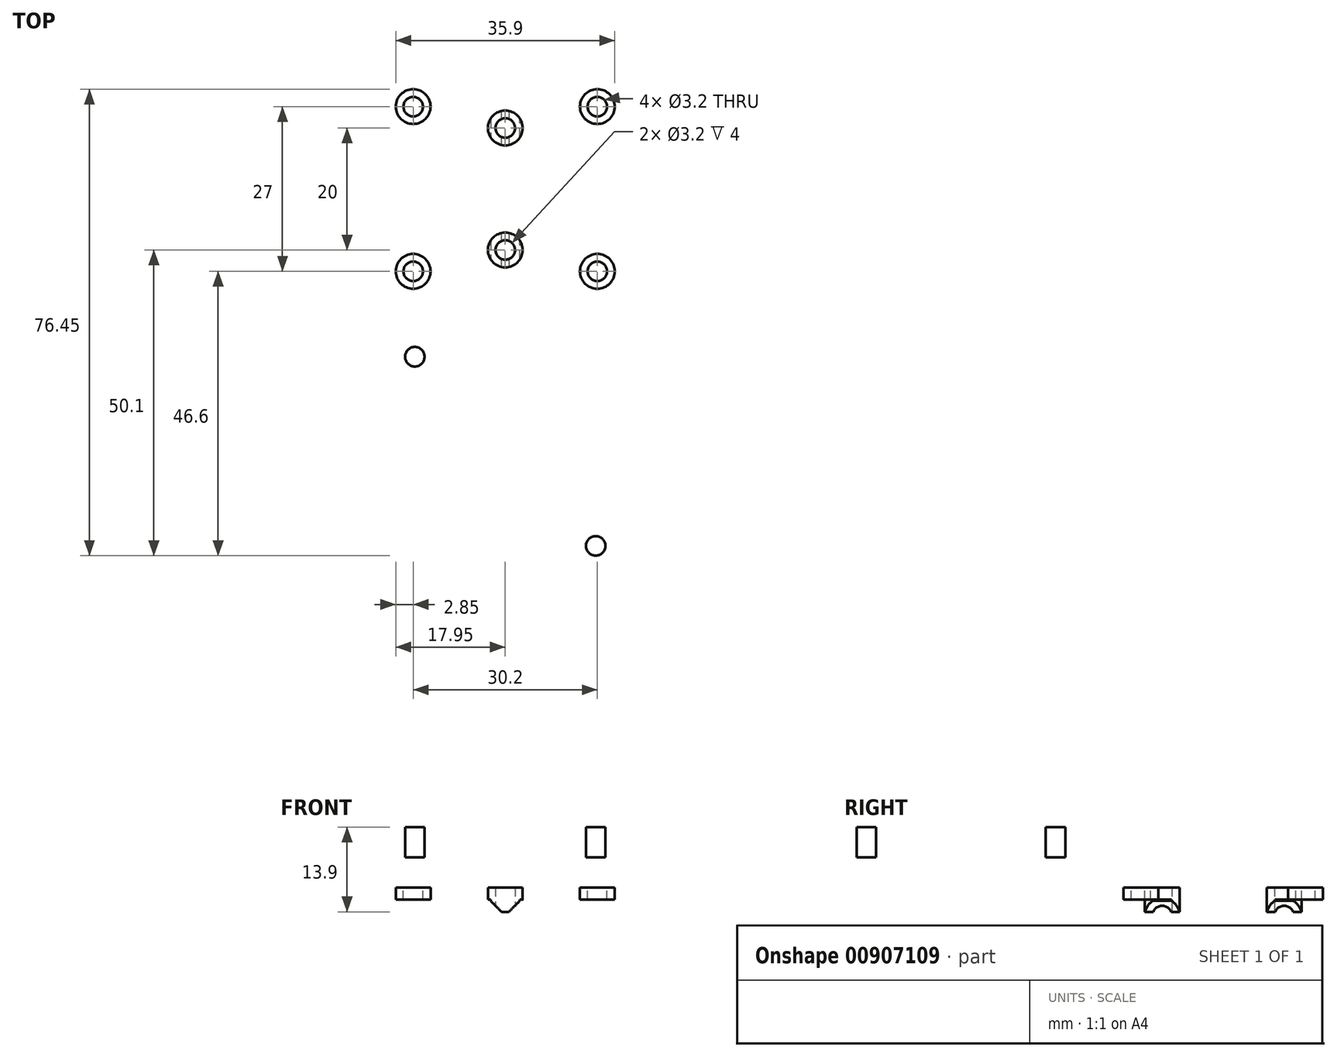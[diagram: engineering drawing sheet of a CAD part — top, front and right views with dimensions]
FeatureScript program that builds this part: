
annotation { "Feature Type Name" : "Feature", "Feature Type Description" : "" }
export const myFeature = defineFeature(function(context is Context, id is Id, definition is map)
    precondition{}
    {
        {
            var Q0;
            Q0=qCreatedBy(makeId("Top.planeOp"),FACE);
            var sketch = newSketch(context, id + "F0", { "sketchPlane" : qUnion([Q0])});
            skLineSegment(sketch, "E0.bottom", {"start": v(0, 0) * mm, "end": v(40.2, 0) * mm});
            skLineSegment(sketch, "E0.top", {"start": v(0, 40) * mm, "end": v(40.2, 40) * mm});
            skLineSegment(sketch, "E0.left", {"start": v(0, 0) * mm, "end": v(0, 40) * mm});
            skLineSegment(sketch, "E0.right", {"start": v(40.2, 0) * mm, "end": v(40.2, 40) * mm});
            skSolve(sketch);
        }
        {
            var Q0;
            Q0=qSketchRegion(id+"F0",true);
            extrude(context, id + "F1", {"entities" : qUnion([Q0]), "depth" : 5.5 * mm, "offsetDistance" : 25 * mm});
        }
        {
            var Q0;
            Q0=makeQuery(id+"F1.opExtrude","CAP_FACE",FACE,{"disambiguationData":[OSD([sQuery(id+"F0.wireOp",EDGE,"E0.bottom"),sQuery(id+"F0.wireOp",EDGE,"E0.top"),sQuery(id+"F0.wireOp",EDGE,"E0.left"),sQuery(id+"F0.wireOp",EDGE,"E0.right")])],"isStart":false});
            var sketch = newSketch(context, id + "F2", { "sketchPlane" : qUnion([Q0])});
            skLineSegment(sketch, "E1", {"start": v(0, 20) * mm, "end": v(40.2, 20) * mm, "construction": true});
            skLineSegment(sketch, "E2", {"start": v(35.2, 40) * mm, "end": v(35.2, 0) * mm, "construction": true});
            skLineSegment(sketch, "E3", {"start": v(0, 6.5) * mm, "end": v(40.2, 6.5) * mm, "construction": true});
            skLineSegment(sketch, "E4", {"start": v(40.2, 33.5) * mm, "end": v(0, 33.5) * mm, "construction": true});
            skCircle(sketch, "E5", {"center": v(35.2, 6.5) * mm, "radius": 2.85 * mm});
            skCircle(sketch, "E6", {"center": v(35.2, 33.5) * mm, "radius": 2.85 * mm});
            skLineSegment(sketch, "E7", {"start": v(20.1, 40) * mm, "end": v(20.1, 0) * mm, "construction": true});
            skCircle(sketch, "E8.MirrorC", {"center": v(5, 33.5) * mm, "radius": 2.85 * mm});
            skCircle(sketch, "E9.MirrorC", {"center": v(5, 6.5) * mm, "radius": 2.85 * mm});
            skSolve(sketch);
        }
        {
            var Q0;
            Q0=qSketchRegion(id+"F2",true);
            extrude(context, id + "F3", {"entities" : qUnion([Q0]), "operationType" : NewBodyOperationType.REMOVE, "oppositeDirection" : true, "depth" : 3.5 * mm, "offsetDistance" : 25 * mm});
        }
        {
            var Q0;
            Q0=makeQuery(id+"F2.imprint","IMPRINT",FACE,{"disambiguationData":[TD([[makeQuery(id+"F2.imprint","IMPRINT",EDGE,{"derivedFrom":sQuery(id+"F2.wireOp",EDGE,"E5")}),-1.0]])]});
            var sketch = newSketch(context, id + "F4", { "sketchPlane" : qUnion([Q0])});
            skCircle(sketch, "E10", {"center": v(35.2, 33.5) * mm, "radius": 1.6 * mm});
            skCircle(sketch, "E11", {"center": v(35.2, 6.5) * mm, "radius": 1.6 * mm});
            skCircle(sketch, "E12.MirrorC", {"center": v(5, 33.5) * mm, "radius": 1.6 * mm});
            skCircle(sketch, "E13.MirrorC", {"center": v(5, 6.5) * mm, "radius": 1.6 * mm});
            skSolve(sketch);
        }
        {
            var Q0;
            Q0=qSketchRegion(id+"F4",true);
            extrude(context, id + "F5", {"entities" : qUnion([Q0]), "operationType" : NewBodyOperationType.REMOVE, "oppositeDirection" : true, "depth" : 25 * mm, "offsetDistance" : 25 * mm});
        }
        {
            var Q0;
            Q0=makeQuery(id+"F1.opExtrude","CAP_FACE",FACE,{"disambiguationData":[OSD([sQuery(id+"F0.wireOp",EDGE,"E0.bottom"),sQuery(id+"F0.wireOp",EDGE,"E0.top"),sQuery(id+"F0.wireOp",EDGE,"E0.left"),sQuery(id+"F0.wireOp",EDGE,"E0.right")])],"isStart":true});
            var sketch = newSketch(context, id + "F6", { "sketchPlane" : qUnion([Q0])});
            skLineSegment(sketch, "E14.bottom", {"start": v(17.7, 0) * mm, "end": v(22.5, 0) * mm});
            skLineSegment(sketch, "E14.top", {"start": v(17.7, -40) * mm, "end": v(22.5, -40) * mm});
            skLineSegment(sketch, "E14.left", {"start": v(22.5, 0) * mm, "end": v(22.5, -40) * mm});
            skLineSegment(sketch, "E14.right", {"start": v(17.7, 0) * mm, "end": v(17.7, -40) * mm});
            skSolve(sketch);
        }
        {
            var Q0;
            Q0=qSketchRegion(id+"F6",true);
            extrude(context, id + "F7", {"entities" : qUnion([Q0]), "operationType" : NewBodyOperationType.ADD, "depth" : 2 * mm, "offsetDistance" : 25 * mm});
        }
        {
            var Q0;
            Q0=makeQuery(id+"F7.opExtrude","CAP_EDGE",EDGE,{"disambiguationData":[OSD([sQuery(id+"F6.wireOp",EDGE,"E14.right")])],"isStart":false});
            var Q1;
            Q1=makeQuery(id+"F7.opExtrude","CAP_EDGE",EDGE,{"disambiguationData":[OSD([sQuery(id+"F6.wireOp",EDGE,"E14.left")])],"isStart":false});
            chamfer(context, id + "F8", {"entities" : qUnion([Q0, Q1]), "width" : 1.8 * mm, "tangentPropagation" : true});
        }
        {
            var Q0;
            Q0=makeQuery(id+"F7.opExtrude","CAP_FACE",FACE,{"disambiguationData":[OSD([sQuery(id+"F6.wireOp",EDGE,"E14.bottom"),sQuery(id+"F6.wireOp",EDGE,"E14.top"),sQuery(id+"F6.wireOp",EDGE,"E14.left"),sQuery(id+"F6.wireOp",EDGE,"E14.right")])],"isStart":false});
            var sketch = newSketch(context, id + "F9", { "sketchPlane" : qUnion([Q0])});
            skCircle(sketch, "E15", {"center": v(20.1, -30) * mm, "radius": 1.6 * mm});
            skLineSegment(sketch, "E16", {"start": v(20.1, 0) * mm, "end": v(20.1, -40) * mm, "construction": true});
            skLineSegment(sketch, "E17", {"start": v(20.7, -30) * mm, "end": v(19.5, -30) * mm, "construction": true});
            skLineSegment(sketch, "E18", {"start": v(20.7, -10) * mm, "end": v(19.5, -10) * mm, "construction": true});
            skPoint(sketch, "E19", {"position": v(20.1, -10) * mm});
            skCircle(sketch, "E20", {"center": v(20.1, -10) * mm, "radius": 1.6 * mm});
            skSolve(sketch);
        }
        {
            var Q0;
            Q0=qSketchRegion(id+"F9",true);
            extrude(context, id + "F10", {"entities" : qUnion([Q0]), "operationType" : NewBodyOperationType.REMOVE, "oppositeDirection" : true, "depth" : 25 * mm, "offsetDistance" : 25 * mm});
        }
        {
            var Q0;
            Q0=makeQuery(id+"F2.imprint","IMPRINT",FACE,{"disambiguationData":[TD([[makeQuery(id+"F2.imprint","IMPRINT",EDGE,{"derivedFrom":sQuery(id+"F2.wireOp",EDGE,"E5")}),-1.0]])]});
            var sketch = newSketch(context, id + "F11", { "sketchPlane" : qUnion([Q0])});
            skCircle(sketch, "E21", {"center": v(20.1, 30) * mm, "radius": 2.85 * mm});
            skCircle(sketch, "E22.MirrorC", {"center": v(20.1, 10) * mm, "radius": 2.85 * mm});
            skSolve(sketch);
        }
        {
            var Q0;
            Q0=qSketchRegion(id+"F11",true);
            extrude(context, id + "F12", {"entities" : qUnion([Q0]), "operationType" : NewBodyOperationType.REMOVE, "oppositeDirection" : true, "depth" : 3.5 * mm, "offsetDistance" : 25 * mm});
        }
        {
            var Q0;
            Q0=makeQuery(id+"F2.imprint","IMPRINT",FACE,{"disambiguationData":[TD([[makeQuery(id+"F2.imprint","IMPRINT",EDGE,{"derivedFrom":sQuery(id+"F2.wireOp",EDGE,"E5")}),-1.0]])]});
            extrude(context, id + "F13", {"entities" : qUnion([Q0]), "operationType" : NewBodyOperationType.ADD, "depth" : 6.4 * mm, "offsetDistance" : 25 * mm});
        }
        {
            var Q0;
            Q0 = qSketchRegion(id + "F11", true);
            extrude(context, id + "F14", {"entities" : qUnion([Q0]), "operationType" : NewBodyOperationType.REMOVE, "oppositeDirection" : true, "depth" : -25 * mm, "offsetDistance" : 25 * mm});
        }
        {
            var Q0;
            {var subQ0=sQuery(id+"F0.wireOp",EDGE,"E0.bottom");Q0=makeQuery(id+"F13.boolean.opBoolean","MERGE",FACE,{"derivedFrom":[makeQuery(id+"F7.boolean.opBoolean","MERGE",FACE,{"derivedFrom":[makeQuery(id+"F1.opExtrude","SWEPT_FACE",FACE,{"disambiguationData":[OSD([subQ0])]}),makeQuery(id+"F7.opExtrude","SWEPT_FACE",FACE,{"disambiguationData":[OSD([sQuery(id+"F6.wireOp",EDGE,"E14.bottom")])]})]}),makeQuery(id+"F13.opExtrude","SWEPT_FACE",FACE,{"disambiguationData":[OSD([subQ0])]})]});}
            var sketch = newSketch(context, id + "F15", { "sketchPlane" : qUnion([Q0])});
            skLineSegment(sketch, "E23.bottom", {"start": v(40.2, 11.9) * mm, "end": v(0, 11.9) * mm});
            skLineSegment(sketch, "E23.top", {"start": v(40.2, 6.9) * mm, "end": v(0, 6.9) * mm});
            skLineSegment(sketch, "E23.left", {"start": v(40.2, 11.9) * mm, "end": v(40.2, 6.9) * mm});
            skLineSegment(sketch, "E23.right", {"start": v(0, 11.9) * mm, "end": v(0, 6.9) * mm});
            skSolve(sketch);
        }
        {
            var Q0;
            Q0=makeQuery(id+"F15.imprint","IMPRINT",FACE,{"disambiguationData":[TD([[makeQuery(id+"F15.imprint","IMPRINT",EDGE,{"derivedFrom":sQuery(id+"F15.wireOp",EDGE,"E23.bottom")}),-1.0]])]});
            extrude(context, id + "F16", {"entities" : qUnion([Q0]), "operationType" : NewBodyOperationType.ADD, "depth" : 44 * mm, "offsetDistance" : 25 * mm});
        }
        {
            var Q0;
            Q0=makeQuery(id+"F16.boolean.opBoolean","MERGE",FACE,{"derivedFrom":[makeQuery(id+"F13.opExtrude","CAP_FACE",FACE,{"disambiguationData":[OSD([sQuery(id+"F0.wireOp",EDGE,"E0.bottom"),sQuery(id+"F0.wireOp",EDGE,"E0.top"),sQuery(id+"F0.wireOp",EDGE,"E0.left"),sQuery(id+"F0.wireOp",EDGE,"E0.right"),sQuery(id+"F2.wireOp",EDGE,"E5"),sQuery(id+"F2.wireOp",EDGE,"E6"),sQuery(id+"F2.wireOp",EDGE,"E8.MirrorC"),sQuery(id+"F2.wireOp",EDGE,"E9.MirrorC")])],"isStart":false}),makeQuery(id+"F16.opExtrude","SWEPT_FACE",FACE,{"disambiguationData":[OSD([sQuery(id+"F15.wireOp",EDGE,"E23.bottom")])]})]});
            var sketch = newSketch(context, id + "F17", { "sketchPlane" : qUnion([Q0])});
            skLineSegment(sketch, "E24", {"start": v(40.2, -2) * mm, "end": v(0, -2) * mm, "construction": true});
            skLineSegment(sketch, "E25", {"start": v(0, -44) * mm, "end": v(40.2, -2) * mm, "construction": true});
            skLineSegment(sketch, "E26", {"start": v(0, -2) * mm, "end": v(40.2, -44) * mm, "construction": true});
            skCircle(sketch, "E27", {"center": v(20.1, -23) * mm, "radius": 11.1 * mm});
            skCircle(sketch, "E28", {"center": v(5.26, -38.5) * mm, "radius": 1.6 * mm});
            skLineSegment(sketch, "E29", {"start": v(40.2, -23) * mm, "end": v(0, -23) * mm, "construction": true});
            skLineSegment(sketch, "E30", {"start": v(20.1, -44) * mm, "end": v(20.1, -2) * mm, "construction": true});
            skCircle(sketch, "E31.MirrorC", {"center": v(34.94, -38.5) * mm, "radius": 1.6 * mm});
            skCircle(sketch, "E32.MirrorC", {"center": v(5.26, -7.5) * mm, "radius": 1.6 * mm});
            skCircle(sketch, "E33.MirrorC", {"center": v(34.94, -7.5) * mm, "radius": 1.6 * mm});
            skSolve(sketch);
        }
        {
            var Q0;
            Q0=makeQuery(id+"F17.imprint","IMPRINT",FACE,{"disambiguationData":[TD([[makeQuery(id+"F17.imprint","IMPRINT",EDGE,{"derivedFrom":sQuery(id+"F17.wireOp",EDGE,"E27")}),1.0]])]});
            var Q1;
            Q1=makeQuery(id+"F17.imprint","IMPRINT",FACE,{"disambiguationData":[TD([[makeQuery(id+"F17.imprint","IMPRINT",EDGE,{"derivedFrom":sQuery(id+"F17.wireOp",EDGE,"E28")}),1.0]])]});
            var Q2;
            Q2=makeQuery(id+"F17.imprint","IMPRINT",FACE,{"disambiguationData":[TD([[makeQuery(id+"F17.imprint","IMPRINT",EDGE,{"derivedFrom":sQuery(id+"F17.wireOp",EDGE,"E31.MirrorC")}),-1.0]])]});
            var Q3;
            Q3=makeQuery(id+"F17.imprint","IMPRINT",FACE,{"disambiguationData":[TD([[makeQuery(id+"F17.imprint","IMPRINT",EDGE,{"derivedFrom":sQuery(id+"F17.wireOp",EDGE,"E32.MirrorC")}),-1.0]])]});
            var Q4;
            Q4=makeQuery(id+"F17.imprint","IMPRINT",FACE,{"disambiguationData":[TD([[makeQuery(id+"F17.imprint","IMPRINT",EDGE,{"derivedFrom":sQuery(id+"F17.wireOp",EDGE,"E33.MirrorC")}),1.0]])]});
            extrude(context, id + "F18", {"entities" : qUnion([Q0, Q1, Q2, Q3, Q4]), "operationType" : NewBodyOperationType.REMOVE, "oppositeDirection" : true, "depth" : 25 * mm, "offsetDistance" : 25 * mm});
        }
    });
